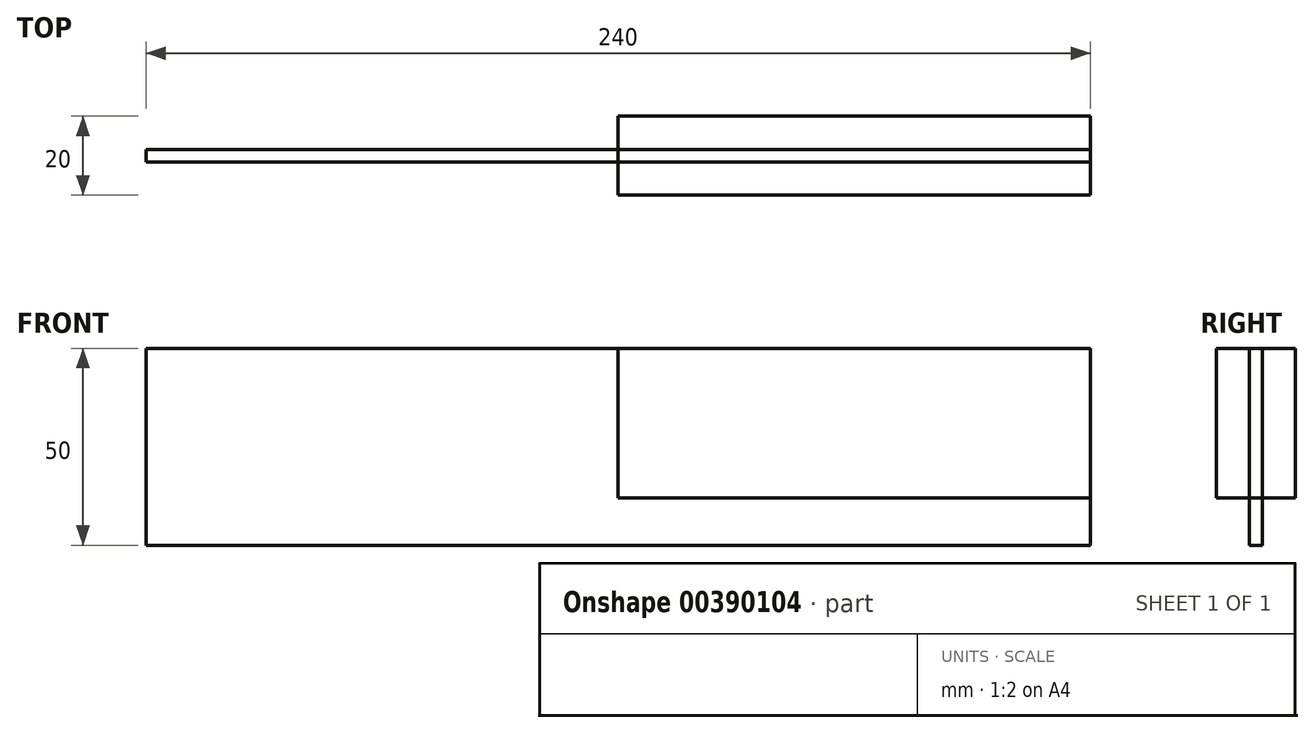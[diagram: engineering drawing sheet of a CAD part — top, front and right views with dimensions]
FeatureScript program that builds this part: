
annotation { "Feature Type Name" : "Feature", "Feature Type Description" : "" }
export const myFeature = defineFeature(function(context is Context, id is Id, definition is map)
    precondition{}
    {
        {
            var Q0;
            Q0=qCreatedBy(makeId("Front.planeOp"),FACE);
            var sketch = newSketch(context, id + "F0", { "sketchPlane" : qUnion([Q0])});
            skLineSegment(sketch, "E0.bottom", {"start": v(0, 0) * mm, "end": v(240, 0) * mm});
            skLineSegment(sketch, "E0.top", {"start": v(0, -50) * mm, "end": v(240, -50) * mm});
            skLineSegment(sketch, "E0.left", {"start": v(0, 0) * mm, "end": v(0, -50) * mm});
            skLineSegment(sketch, "E0.right", {"start": v(240, 0) * mm, "end": v(240, -50) * mm});
            skSolve(sketch);
        }
        {
            var Q0;
            Q0=makeQuery(id+"F0.imprint","IMPRINT",FACE,{"disambiguationData":[TD([[makeQuery(id+"F0.imprint","IMPRINT",EDGE,{"derivedFrom":sQuery(id+"F0.wireOp",EDGE,"E0.bottom")}),-1.0]])]});
            var sketch = newSketch(context, id + "F1", { "sketchPlane" : qUnion([Q0])});
            skLineSegment(sketch, "E1.bottom", {"start": v(120, 0) * mm, "end": v(240, 0) * mm});
            skLineSegment(sketch, "E1.top", {"start": v(120, -38) * mm, "end": v(240, -38) * mm});
            skLineSegment(sketch, "E1.left", {"start": v(120, 0) * mm, "end": v(120, -38) * mm});
            skLineSegment(sketch, "E1.right", {"start": v(240, 0) * mm, "end": v(240, -38) * mm});
            skSolve(sketch);
        }
        {
            var Q0;
            Q0=qSketchRegion(id+"F0",true);
            extrude(context, id + "F2", {"entities" : qUnion([Q0]), "endBound" : BoundingType.SYMMETRIC, "depth" : 3.2 * mm});
        }
        {
            var Q0;
            Q0=qSketchRegion(id+"F1",true);
            extrude(context, id + "F3", {"entities" : qUnion([Q0]), "endBound" : BoundingType.SYMMETRIC, "depth" : 20 * mm});
        }
    });
